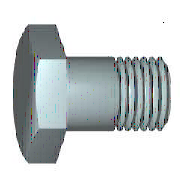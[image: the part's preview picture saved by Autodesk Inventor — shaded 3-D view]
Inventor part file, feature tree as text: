
AUTODESK INVENTOR PART (.ipt)
format: ipt  version: 2020 (Build 240168000, 168)  size: 200,192 bytes
history: native  units: mm (DEFAULTED — no unit token found)
features: sketch x3, extrude x1, chamfer x1, plane x1
ambient origin geometry x7: Origin, YZ Plane, XZ Plane, X Axis, Y Axis, Z Axis, Center Point
bodies: Solid1 (feature_tree), Body (feature_tree)
feature tree (6):
  extrude  "Head"  Depth=13.0mm
  chamfer  "Chamfer1"  Distance=3.5mm
  plane  "Work Plane1"
  sketch  "Sketch1"  dims[d0=16.0mm d1=13.0mm]
  sketch  "Sketch2"  dims[d2=6.0mm]
  sketch  "Sketch4"  dims[d12=90.0deg d3=3.5mm d4=0.0mm d5=30.0deg d21=90.0deg d6=0.61345mm d7=0.61355mm d8=0.0mm d9=0.5001mm d10=10.0mm d11=10.0mm d13=0.61355mm d14=6.0mm d15=13.0mm d16=0.0mm d19=10.0mm d55=45.0deg d57=0.0mm d58=0.0mm]
